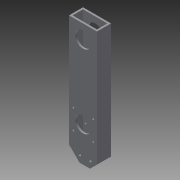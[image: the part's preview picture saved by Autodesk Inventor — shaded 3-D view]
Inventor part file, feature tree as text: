
AUTODESK INVENTOR PART (.ipt)
format: ipt  version: 2013 (Build 170138000, 138)  size: 179,712 bytes
history: native  units: in
note: dims shown in document units (in); Inventor stores cm internally (conversion verified against a paired STEP export)
features: extrude x8, sketch x8
ambient origin geometry x8: Origin, YZ Plane, XZ Plane, XY Plane, X Axis, Y Axis, Z Axis, Center Point
bodies: Solid1 (feature_tree)
feature tree (16):
  extrude  "Extrusion1"  Depth=1.0in
  extrude  "Extrusion2"  Depth=0.75in
  extrude  "Extrusion3"  Depth=1.0in
  extrude  "Extrusion4"  Depth=7.0in
  extrude  "Extrusion5"  Depth=0.25in
  extrude  "Extrusion6"  Depth=0.5in
  extrude  "Extrusion7"  TaperAngle=0.0deg  [1 undecoded]
  extrude  "Extrusion8"  Depth=0.2in
  sketch  "Sketch1"  dims[d0=2.0in d1=1.0in]
  sketch  "Sketch2"  dims[d2=1.75in d3=0.75in]
  sketch  "Sketch3"  dims[d4=9.0in d5=0.0in d6=1.0in]
  sketch  "Sketch4"  dims[d7=0.5in d8=7.0in]
  sketch  "Sketch5"  dims[d9=90.0deg d10=0.25in]
  sketch  "Sketch6"  dims[d11=90.0deg d12=0.5in]
  sketch  "Sketch7"  dims[d13=0.75in d14=0.0in]
  sketch  "Sketch8"  dims[d15=0.2in d16=0.2in d17=9.0in d18=0.0in d19=0.25in d20=0.0in d21=25.0in d22=0.0in d23=25.0in d24=0.0in d25=2.5in d26=90.0deg d27=0.75in d28=1.0in d29=45.0deg d30=2.0in d31=0.16in d32=0.16in d33=0.16in d34=0.16in d35=25.0in d36=0.0in d37=1.125in d38=25.0in d39=0.0in d40=1.125in d41=1.0in d42=0.0in]
note: 1 required parameter value undecoded (feature->parameter linkage not recoverable at this tier; creation-order binding heuristic only, values carry confidence <= 0.55)
